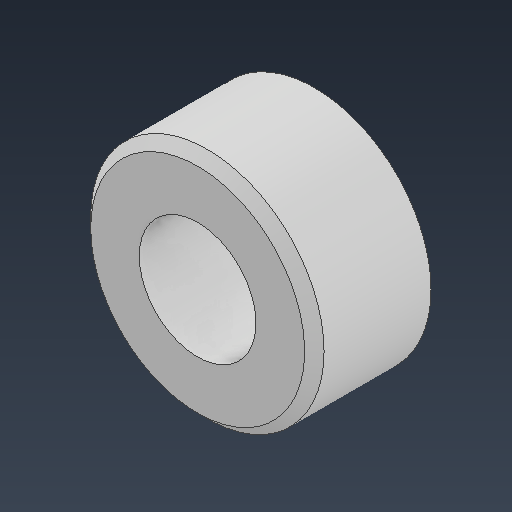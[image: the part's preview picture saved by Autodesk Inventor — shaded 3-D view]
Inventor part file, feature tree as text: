
AUTODESK INVENTOR PART (.ipt)
format: ipt  version: 2021 (Build 250183000, 183)  size: 96,256 bytes
history: native  units: in
note: dims shown in document units (in); Inventor stores cm internally (conversion verified against a paired STEP export)
features: chamfer x1
ambient origin geometry x8: Origin, YZ Plane, XZ Plane, XY Plane, X Axis, Y Axis, Z Axis, Center Point
bodies: Solid1 (feature_tree)
feature tree (1):
  chamfer  "Chamfer1"  [1 undecoded]
note: 1 required parameter value undecoded (feature->parameter linkage not recoverable at this tier; creation-order binding heuristic only, values carry confidence <= 0.55)
